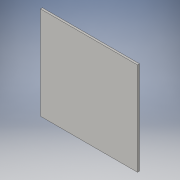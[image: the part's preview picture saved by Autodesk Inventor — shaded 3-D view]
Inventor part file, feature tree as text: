
AUTODESK INVENTOR PART (.ipt)
format: ipt  version: 2016 (Build 200138000, 138)  size: 84,480 bytes
history: native  units: in
note: dims shown in document units (in); Inventor stores cm internally (conversion verified against a paired STEP export)
features: extrude x1, sketch x1
ambient origin geometry x8: Origin, YZ Plane, XZ Plane, XY Plane, X Axis, Y Axis, Z Axis, Center Point
bodies: Solid1 (feature_tree)
feature tree (2):
  extrude  "Extrusion1"  Depth=2.3in
  sketch  "Sketch1"  dims[d0=2.4in d1=2.3in d2=0.05in d3=0.0in]
